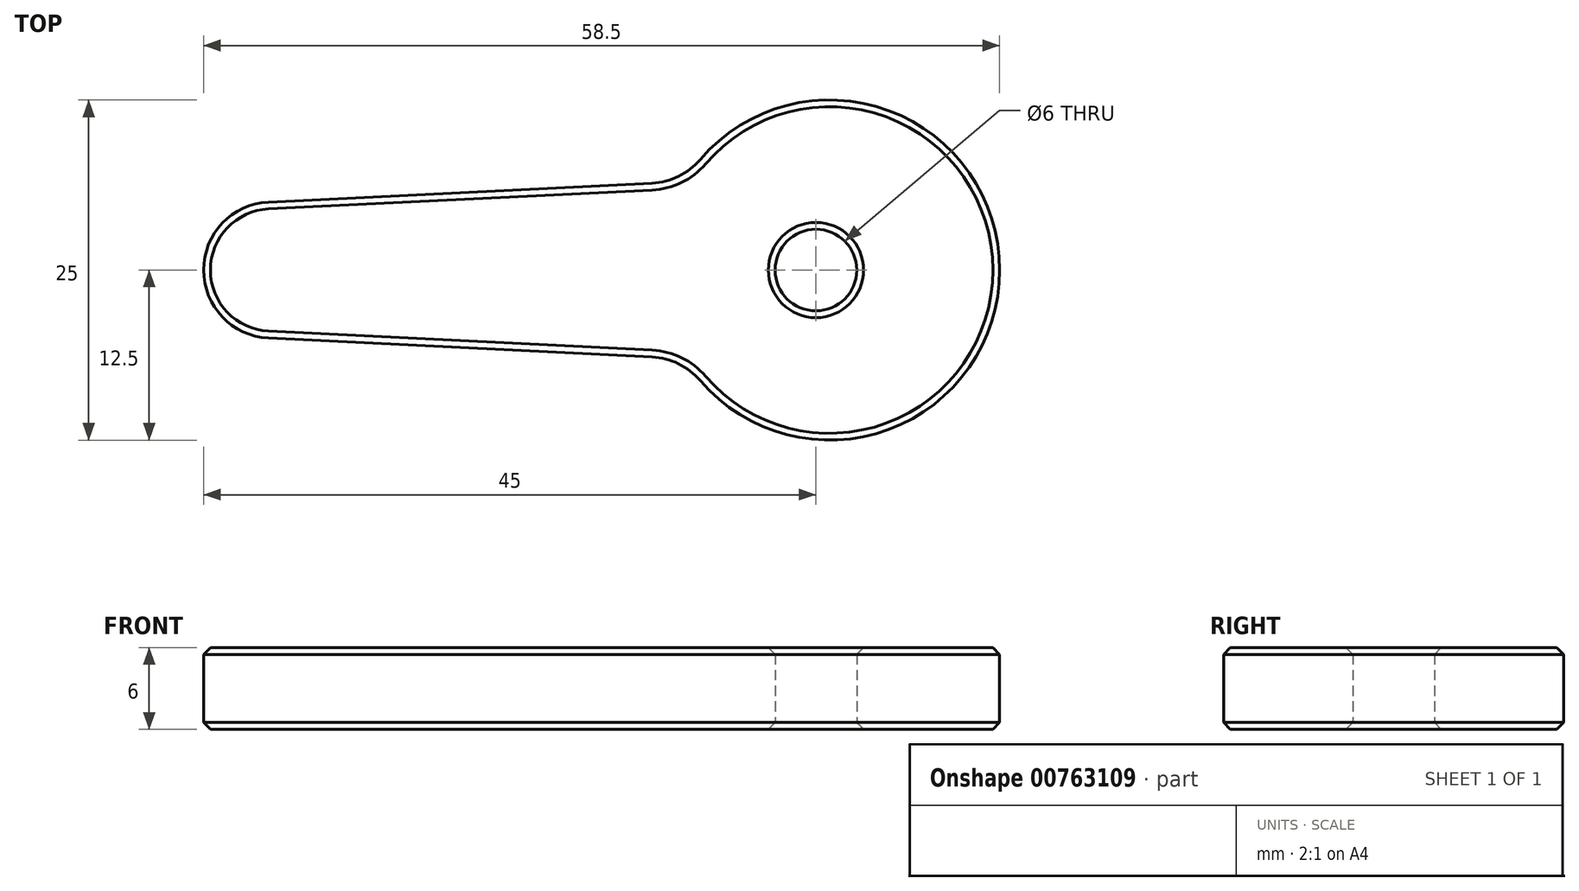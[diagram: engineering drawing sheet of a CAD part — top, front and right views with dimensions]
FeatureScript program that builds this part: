
annotation { "Feature Type Name" : "Feature", "Feature Type Description" : "" }
export const myFeature = defineFeature(function(context is Context, id is Id, definition is map)
    precondition{}
    {
        {
            var Q0;
            Q0=qCreatedBy(makeId("Top.planeOp"),FACE);
            var sketch = newSketch(context, id + "F0", { "sketchPlane" : qUnion([Q0])});
            skCircle(sketch, "E0", {"center": v(0, 0) * mm, "radius": 3 * mm});
            skArc(sketch, "E1", {"start": v(-8.5, -8.13) * mm, "mid": v(13.5, 0) * mm, "end": v(-8.5, 8.13) * mm});
            skArc(sketch, "E2", {"start": v(-40.25, 5) * mm, "mid": v(-45, 0) * mm, "end": v(-40.25, -5) * mm});
            skLineSegment(sketch, "E3", {"start": v(-40.25, 5) * mm, "end": v(-12.05, 6.38) * mm});
            skLineSegment(sketch, "E4", {"start": v(-40.25, -5) * mm, "end": v(-12.05, -6.38) * mm});
            skLineSegment(sketch, "E5", {"start": v(1, 0) * mm, "end": v(1, 9.23) * mm, "construction": true});
            skPoint(sketch, "E6.visualSharp", {"position": v(-9.68, 6.5) * mm});
            skArc(sketch, "E6.filletArc", {"start": v(-12.05, 6.38) * mm, "mid": v(-10.1, 6.89) * mm, "end": v(-8.5, 8.13) * mm});
            skPoint(sketch, "E7.visualSharp", {"position": v(-9.68, -6.5) * mm});
            skArc(sketch, "E7.filletArc", {"start": v(-8.5, -8.13) * mm, "mid": v(-10.1, -6.89) * mm, "end": v(-12.05, -6.38) * mm});
            skSolve(sketch);
        }
        {
            var Q0;
            Q0=makeQuery(id+"F0.imprint","IMPRINT",FACE,{"disambiguationData":[TD([[makeQuery(id+"F0.imprint","IMPRINT",EDGE,{"derivedFrom":sQuery(id+"F0.wireOp",EDGE,"E0")}),-1.0]])]});
            extrude(context, id + "F1", {"entities" : qUnion([Q0]), "depth" : 6 * mm, "offsetDistance" : 25 * mm});
        }
        {
            var Q0;
            Q0=makeQuery(id+"F1.opExtrude","CAP_EDGE",EDGE,{"disambiguationData":[OSD([sQuery(id+"F0.wireOp",EDGE,"E3")])],"isStart":false});
            var Q1;
            Q1=makeQuery(id+"F1.opExtrude","CAP_EDGE",EDGE,{"disambiguationData":[OSD([sQuery(id+"F0.wireOp",EDGE,"E4")])],"isStart":true});
            var Q2;
            Q2=makeQuery(id+"F1.opExtrude","CAP_EDGE",EDGE,{"disambiguationData":[OSD([sQuery(id+"F0.wireOp",EDGE,"E0")])],"isStart":true});
            var Q3;
            Q3=makeQuery(id+"F1.opExtrude","CAP_EDGE",EDGE,{"disambiguationData":[OSD([sQuery(id+"F0.wireOp",EDGE,"E0")])],"isStart":false});
            chamfer(context, id + "F2", {"entities" : qUnion([Q0, Q1, Q2, Q3]), "width" : 0.5 * mm, "tangentPropagation" : true});
        }
    });
